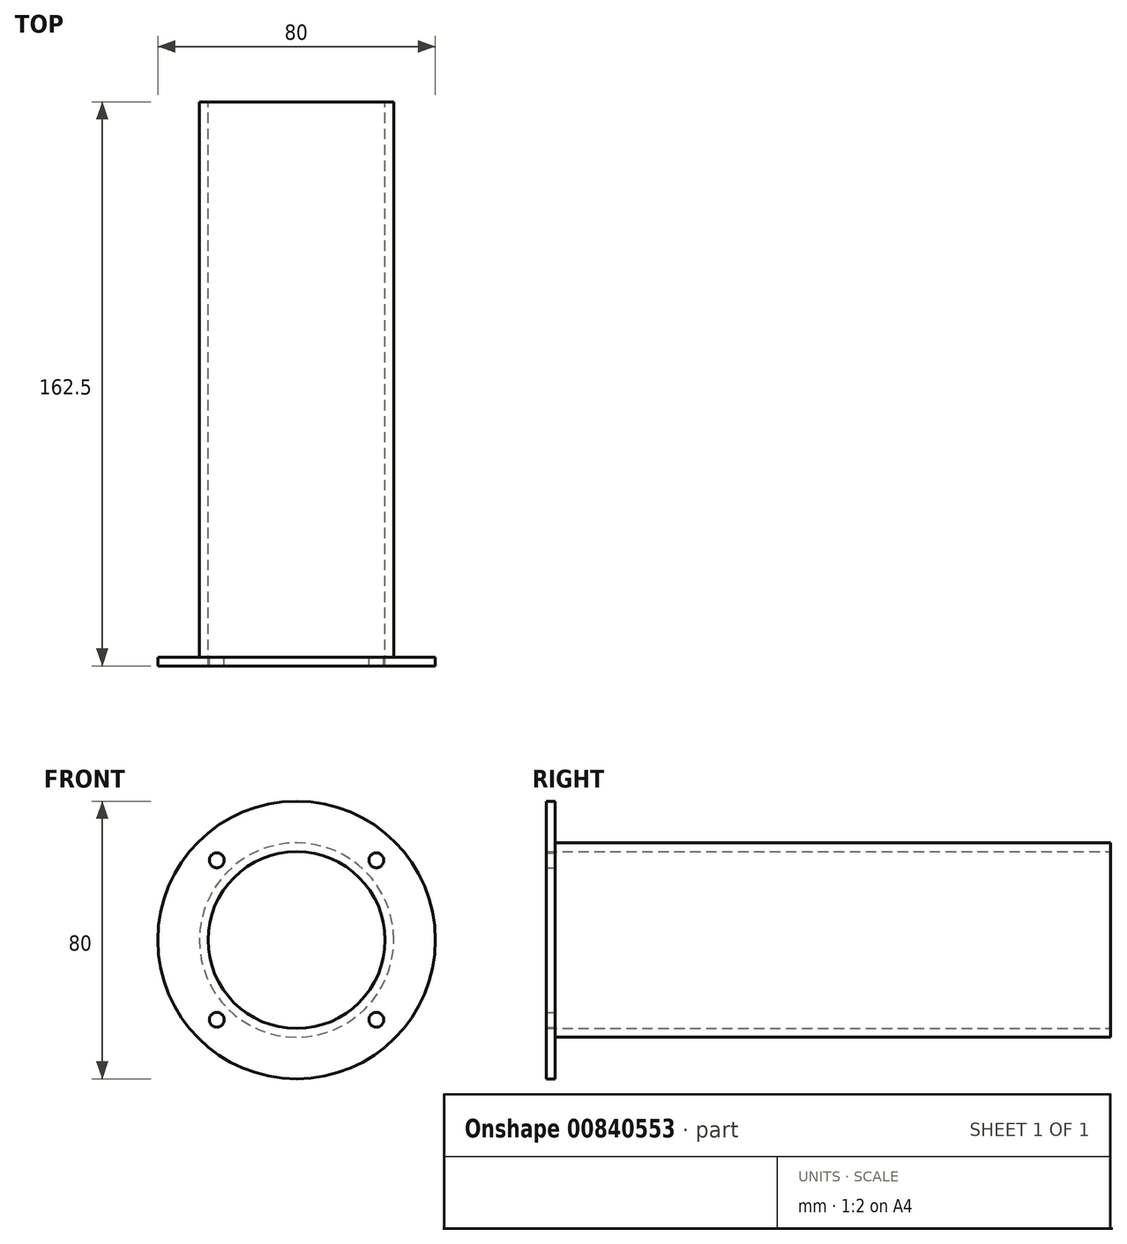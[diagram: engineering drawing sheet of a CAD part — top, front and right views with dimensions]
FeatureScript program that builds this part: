
annotation { "Feature Type Name" : "Feature", "Feature Type Description" : "" }
export const myFeature = defineFeature(function(context is Context, id is Id, definition is map)
    precondition{}
    {
        {
            var Q0;
            Q0=qCreatedBy(makeId("Front.planeOp"),FACE);
            var sketch = newSketch(context, id + "F0", { "sketchPlane" : qUnion([Q0])});
            skCircle(sketch, "E0", {"center": v(0, 0) * mm, "radius": 40 * mm});
            skCircle(sketch, "E1", {"center": v(0, 0) * mm, "radius": 25.5 * mm});
            skCircle(sketch, "E2", {"center": v(0, 0) * mm, "radius": 32.5 * mm});
            skCircle(sketch, "E3", {"center": v(0, 0) * mm, "radius": 28 * mm});
            skLineSegment(sketch, "E4", {"start": v(0, 0) * mm, "end": v(-22.98, 22.98) * mm, "construction": true});
            skLineSegment(sketch, "E5", {"start": v(0, 0) * mm, "end": v(22.98, 22.98) * mm, "construction": true});
            skLineSegment(sketch, "E6", {"start": v(0, 0) * mm, "end": v(-22.98, -22.98) * mm, "construction": true});
            skLineSegment(sketch, "E7", {"start": v(0, 0) * mm, "end": v(22.98, -22.98) * mm, "construction": true});
            skCircle(sketch, "E8", {"center": v(22.98, 22.98) * mm, "radius": 2.15 * mm});
            skCircle(sketch, "E9", {"center": v(22.98, -22.98) * mm, "radius": 2.15 * mm});
            skCircle(sketch, "E10", {"center": v(-22.98, -22.98) * mm, "radius": 2.15 * mm});
            skCircle(sketch, "E11", {"center": v(-22.98, 22.98) * mm, "radius": 2.15 * mm});
            skSolve(sketch);
        }
        {
            var Q0;
            Q0 = qSketchRegion(id + "F0", true);
            var Q1;
            Q1=makeQuery(id+"F0.imprint","IMPRINT",FACE,{"disambiguationData":[TD([[makeQuery(id+"F0.imprint","IMPRINT",EDGE,{"derivedFrom":sQuery(id+"F0.wireOp",EDGE,"E1")}),-1.0]])]});
            var Q2;
            Q2=makeQuery(id+"F0.imprint","IMPRINT",FACE,{"disambiguationData":[TD([[makeQuery(id+"F0.imprint","IMPRINT",EDGE,{"derivedFrom":sQuery(id+"F0.wireOp",EDGE,"E3")}),1.0]])]});
            var Q3;
            Q3=makeQuery(id+"F0.imprint","IMPRINT",FACE,{"disambiguationData":[TD([[makeQuery(id+"F0.imprint","IMPRINT",EDGE,{"derivedFrom":sQuery(id+"F0.wireOp",EDGE,"E3")}),-1.0]])]});
            extrude(context, id + "F1", {"entities" : qUnion([Q0, Q1, Q2, Q3]), "depth" : 2.5 * mm, "offsetDistance" : 25 * mm});
        }
        {
            var Q0;
            Q0=makeQuery(id+"F0.imprint","IMPRINT",FACE,{"disambiguationData":[TD([[makeQuery(id+"F0.imprint","IMPRINT",EDGE,{"derivedFrom":sQuery(id+"F0.wireOp",EDGE,"E1")}),-1.0]])]});
            extrude(context, id + "F2", {"entities" : qUnion([Q0]), "operationType" : NewBodyOperationType.ADD, "depth" : -160 * mm, "offsetDistance" : 25 * mm});
        }
    });
